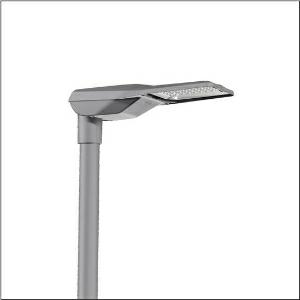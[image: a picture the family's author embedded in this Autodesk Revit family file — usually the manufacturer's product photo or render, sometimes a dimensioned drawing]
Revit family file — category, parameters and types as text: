
# Revit family: streetlight_sl_21_iq_mini___stw1_0a_5xe2e41d08gb_3fc6
name_source: partatom
category: Lighting Fixtures
units: mm (PartAtom-declared; Revit-internal decimal feet)

## family parameters
Cut with Voids When Loaded = No
Host = Face
Light Source = No
Part Type = Normal
Room Calculation Point = No
Round Connector Dimension = Use Diameter
Shared = No

## types (1)
- --- (1 x LED, 5920 lm, 37.1 W, 4000K)
    Apparent Load = 37 VA
    CIE Flux Codes = 38 75 98 100 100
    Color Rendering = 70
    Color Temperature = 4000K
    Default Elevation = 1800 mm
    Description = Streetlight SL 21 iQ mini, mast luminaire, primary light control with lens, of PMMA, primary optical cover: cover, of toughened safety glass, transparent, light distribution: STW1.0a, light emission: direct distribution, primary light characteristic: asymmetric, installation type: post-top, side-entry, LED, High Power LED, rated luminous flux: 5.920lm, luminous efficacy: 160lm/W, light colour: 740, colour temperature: 4000K, control gear: iQ-Comfort, control: Auto-Match, Temp-Guard, Lumen-Switch, Night-Set, Smart-Wire, Light-Fading, Desk-Remote (wireless, voltage-free reading and setting of iQ features in the workshop via application-optimized NFC function/RFID function), optimised constant luminous flux control (CLO 2.0), pre-setting: linear dimming characteristic, mains connection: 220..240V, AC, 50/60Hz, start of lifetime: 37W, end of service life: 39W, reduction: 18W, luminaire housing, of diecast aluminium, powder-coated, Siteco® metallic grey (DB 702S), corrosivity category C5 mid according to DIN EN ISO 12944, please order mast flange separately, inclination adjustable: 0°, 5°, 10°, 15°, sealing non-destructively replaceable, multi-level sealing system, length: 628mm, width: 235mm, height: 110mm, mast flange for spigot size: 42mm (side-entry): 5XC10008XM4, 60/48mm (side-entry/post-top): 5XC10108XM2, 76/60mm (side-entry/post-top): 5XC10108XM1, mounting height: 4..8m, protection rating (complete): IP66, insulation class (complete): insulation class II (safety insulation), certification: CE, ENEC, ENEC+, VDE, impact resistance: IK10, permissible operating ambient temperature for outdoor applications: -40..+50°C, standard-compliant lighting for roads and squares, packaging unit: 1 piece

Light Distribution: STW1.0a
    Height = 110 mm
    Lamp = 1 x LED
    Lamp Light Flux = 5920 lm
    Lamp Power = 37.1 W
    Lamp count = 1
    Length = 625 mm
    Luminous efficacy = 160 lm/W
    Manufacturer = Siteco
    ModVariant = No
    Model = 5XE2E41D08GB
    Number of Poles = 1
    OnlyDefault = Yes
    Power Factor = 1
    Product Name = Streetlight SL 21 iQ mini | STW1.0a
    Product group = mast luminaire | pylon top
    ProductGroupID = 6100
    Protection Class = Protection class II
    Protection Degree = IP 66
    RLX_Detail_Level = 1
    RLX_Emergency_Light_Flux = 0 lm
    RLX_Emergency_Type = 0
    RLX_Emergency_Type_DB = No
    RlxData = <blob elided: 26381 chars, md5=1bf0f255>
    Socket = socket
    Standby Power = 0 W
    System Light Flux = 5920 lm
    System Power = 37 W
    Type Comments = factory setting: luminous flux: 100 % | dim-lin: 254 | 385 mA
    Type Image = l_1003519.jpg
    URL = http://relux.com
    VarID = @adj_208821
    Voltage = 0 V
    Weight = 0.00 kg
    Width = 234 mm

## geometry (parser evidence)
native form markers: Blend x4, Sweep x10
no freeform markers — native parametric forms only
